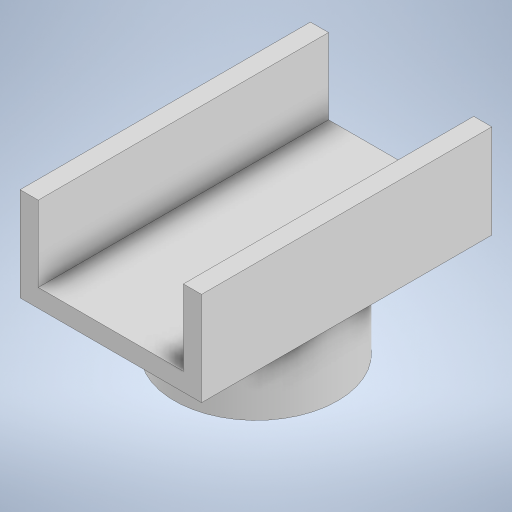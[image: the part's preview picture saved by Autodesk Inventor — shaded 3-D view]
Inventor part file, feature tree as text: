
AUTODESK INVENTOR PART (.ipt)
format: ipt  version: 2024 (Build 280153000, 153)  size: 235,520 bytes
history: native  units: mm
features: extrude x3, other x1, sketch x1, projected_geometry x1
ambient origin geometry x8: Origin, YZ Plane, XZ Plane, XY Plane, X Axis, Y Axis, Z Axis, Center Point
bodies: Body1 (feature_tree)
feature tree (6):
  other  "솔리드1"
  extrude  "돌출1"  Depth=4.8mm
  extrude  "돌출2"  Depth=9.6mm
  extrude  "돌출5"  Depth=0.6mm TaperAngle=0.0deg
  sketch  "스케치2"
  projected_geometry  "투영된 루프1"
